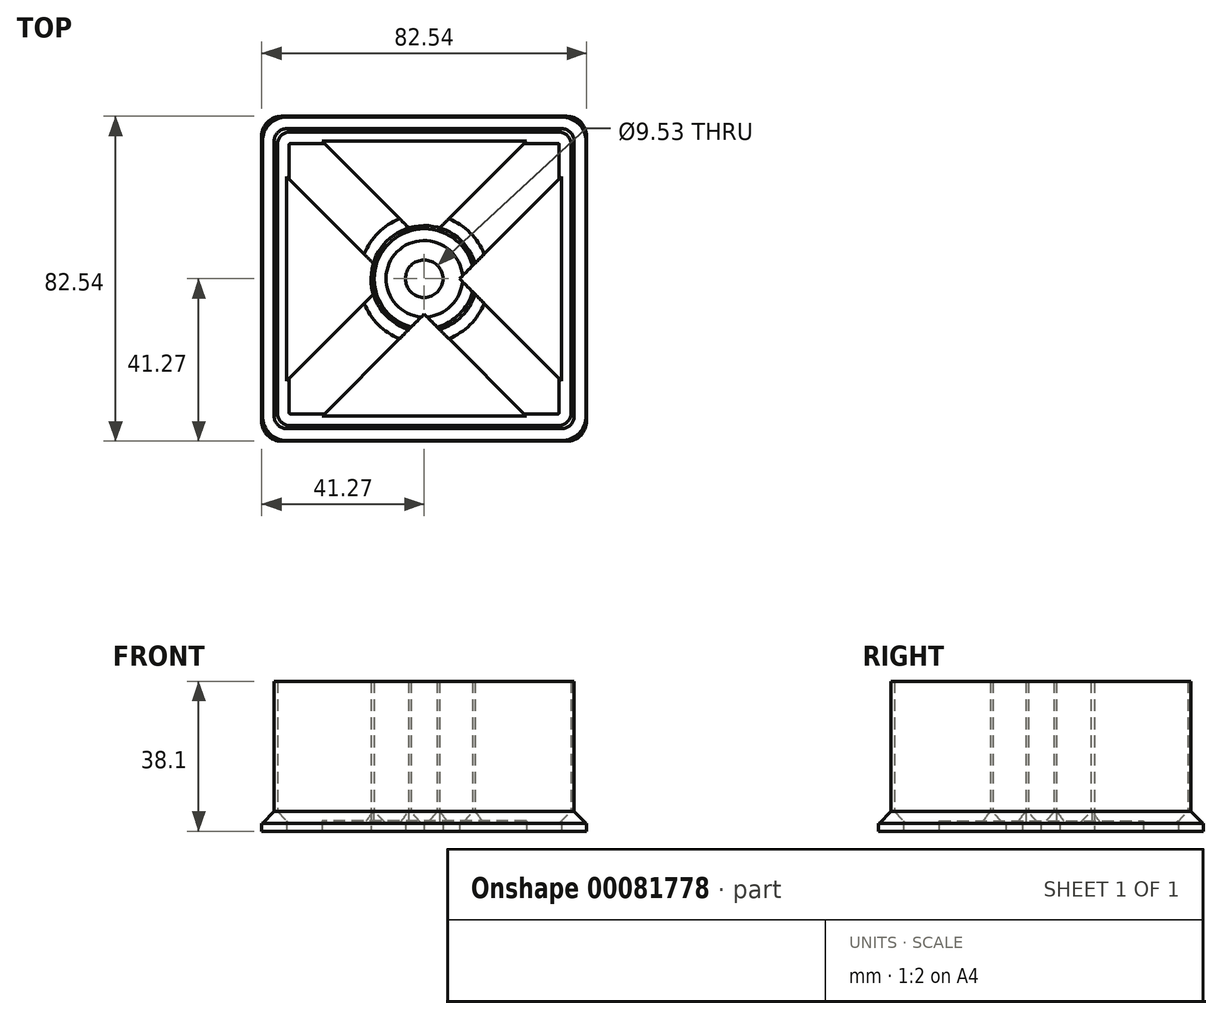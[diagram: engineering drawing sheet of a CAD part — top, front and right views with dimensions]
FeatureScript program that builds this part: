
annotation { "Feature Type Name" : "Feature", "Feature Type Description" : "" }
export const myFeature = defineFeature(function(context is Context, id is Id, definition is map)
    precondition{}
    {
        {
            var Q0;
            Q0=qCreatedBy(makeId("Top.planeOp"),FACE);
            var sketch = newSketch(context, id + "F0", { "sketchPlane" : qUnion([Q0])});
            skLineSegment(sketch, "E0.bottom", {"start": v(-34.92, 38.1) * mm, "end": v(34.93, 38.1) * mm});
            skLineSegment(sketch, "E0.top", {"start": v(-34.93, -38.1) * mm, "end": v(34.92, -38.1) * mm});
            skLineSegment(sketch, "E0.left", {"start": v(-38.1, 34.93) * mm, "end": v(-38.1, -34.93) * mm});
            skLineSegment(sketch, "E0.right", {"start": v(38.1, 34.93) * mm, "end": v(38.1, -34.93) * mm});
            skPoint(sketch, "E0.middle", {"position": v(0, 0) * mm});
            skCircle(sketch, "E1", {"center": v(0, 0) * mm, "radius": 12.7 * mm});
            skLineSegment(sketch, "E2.0", {"start": v(-37.3, 34.13) * mm, "end": v(-37.3, -34.13) * mm});
            skLineSegment(sketch, "E2.1", {"start": v(-34.13, 37.3) * mm, "end": v(34.13, 37.3) * mm});
            skLineSegment(sketch, "E2.2", {"start": v(37.3, 34.13) * mm, "end": v(37.3, -34.13) * mm});
            skLineSegment(sketch, "E2.3", {"start": v(-34.13, -37.3) * mm, "end": v(34.13, -37.3) * mm});
            skCircle(sketch, "E3.0", {"center": v(0, 0) * mm, "radius": 13.5 * mm});
            skLineSegment(sketch, "E4.0", {"start": v(-41.27, 41.27) * mm, "end": v(-41.28, -41.27) * mm});
            skLineSegment(sketch, "E4.1", {"start": v(-41.27, 41.27) * mm, "end": v(41.28, 41.27) * mm});
            skLineSegment(sketch, "E4.2", {"start": v(41.28, 41.27) * mm, "end": v(41.27, -41.27) * mm});
            skLineSegment(sketch, "E4.3", {"start": v(-41.28, -41.27) * mm, "end": v(41.27, -41.27) * mm});
            skLineSegment(sketch, "E5.0", {"start": v(-34.92, 34.92) * mm, "end": v(-34.93, -34.92) * mm});
            skLineSegment(sketch, "E5.1", {"start": v(-34.92, 34.92) * mm, "end": v(34.93, 34.92) * mm});
            skLineSegment(sketch, "E5.2", {"start": v(34.93, 34.92) * mm, "end": v(34.92, -34.92) * mm});
            skLineSegment(sketch, "E5.3", {"start": v(-34.93, -34.92) * mm, "end": v(34.92, -34.92) * mm});
            skLineSegment(sketch, "E6", {"start": v(-34.92, 34.92) * mm, "end": v(34.92, -34.92) * mm, "construction": true});
            skLineSegment(sketch, "E7.trimOffspring", {"start": v(-34.92, 25.94) * mm, "end": v(25.94, -34.92) * mm});
            skLineSegment(sketch, "E8.trimOffspring", {"start": v(-25.94, 34.92) * mm, "end": v(34.92, -25.94) * mm});
            skLineSegment(sketch, "E9", {"start": v(-34.92, -34.92) * mm, "end": v(34.92, 34.92) * mm, "construction": true});
            skLineSegment(sketch, "E10.0", {"start": v(-25.94, -34.93) * mm, "end": v(34.93, 25.94) * mm});
            skLineSegment(sketch, "E11.0", {"start": v(-34.93, -25.94) * mm, "end": v(25.94, 34.93) * mm});
            skCircle(sketch, "E12", {"center": v(0, 0) * mm, "radius": 4.76 * mm});
            skPoint(sketch, "E13.visualSharp", {"position": v(-38.1, -38.1) * mm});
            skArc(sketch, "E13.filletArc", {"start": v(-38.1, -34.93) * mm, "mid": v(-37.17, -37.17) * mm, "end": v(-34.93, -38.1) * mm});
            skPoint(sketch, "E14.visualSharp", {"position": v(-37.3, -37.3) * mm});
            skArc(sketch, "E14.filletArc", {"start": v(-37.3, -34.13) * mm, "mid": v(-36.38, -36.38) * mm, "end": v(-34.13, -37.3) * mm});
            skPoint(sketch, "E15.visualSharp", {"position": v(37.3, -37.3) * mm});
            skArc(sketch, "E15.filletArc", {"start": v(34.13, -37.3) * mm, "mid": v(36.38, -36.38) * mm, "end": v(37.3, -34.13) * mm});
            skPoint(sketch, "E16.visualSharp", {"position": v(38.1, -38.1) * mm});
            skArc(sketch, "E16.filletArc", {"start": v(34.92, -38.1) * mm, "mid": v(37.17, -37.17) * mm, "end": v(38.1, -34.93) * mm});
            skPoint(sketch, "E17.visualSharp", {"position": v(-37.3, 37.3) * mm});
            skArc(sketch, "E17.filletArc", {"start": v(-34.13, 37.3) * mm, "mid": v(-36.38, 36.38) * mm, "end": v(-37.3, 34.13) * mm});
            skPoint(sketch, "E18.visualSharp", {"position": v(-38.1, 38.1) * mm});
            skArc(sketch, "E18.filletArc", {"start": v(-34.92, 38.1) * mm, "mid": v(-37.17, 37.17) * mm, "end": v(-38.1, 34.93) * mm});
            skPoint(sketch, "E19.visualSharp", {"position": v(37.3, 37.3) * mm});
            skArc(sketch, "E19.filletArc", {"start": v(37.3, 34.13) * mm, "mid": v(36.38, 36.38) * mm, "end": v(34.13, 37.3) * mm});
            skPoint(sketch, "E20.visualSharp", {"position": v(38.1, 38.1) * mm});
            skArc(sketch, "E20.filletArc", {"start": v(38.1, 34.93) * mm, "mid": v(37.17, 37.17) * mm, "end": v(34.93, 38.1) * mm});
            skSolve(sketch);
        }
        {
            var Q0;
            Q0 = qSketchRegion(id + "F0", true);
            var Q1;
            {var subQ0=sQuery(id+"F0.wireOp",EDGE,"E7.trimOffspring");var subQ3=sQuery(id+"F0.wireOp",EDGE,"E3.0");var subQ4=makeQuery(id+"F0.imprint","INTERSECT",VERTEX,{"disambiguationData":[OD(1.0)],"derivedFrom":[subQ3,subQ0]});Q1=makeQuery(id+"F0.imprint","IMPRINT",FACE,{"disambiguationData":[TD([[makeQuery(id+"F0.imprint","IMPRINT",EDGE,{"disambiguationData":[TD([[subQ4,-1.0]])],"derivedFrom":subQ3}),-1.0]])]});}
            var Q2;
            {var subQ5=sQuery(id+"F0.wireOp",EDGE,"E3.0");var subQ7=sQuery(id+"F0.wireOp",EDGE,"E7.trimOffspring");var subQ9=makeQuery(id+"F0.imprint","INTERSECT",VERTEX,{"disambiguationData":[OD(0.0)],"derivedFrom":[subQ5,subQ7]});Q2=makeQuery(id+"F0.imprint","IMPRINT",FACE,{"disambiguationData":[TD([[makeQuery(id+"F0.imprint","IMPRINT",EDGE,{"disambiguationData":[TD([[subQ9,1.0]])],"derivedFrom":subQ5}),-1.0]])]});}
            var Q3;
            Q3=makeQuery(id+"F0.imprint","IMPRINT",FACE,{"disambiguationData":[TD([[makeQuery(id+"F0.imprint","IMPRINT",EDGE,{"derivedFrom":sQuery(id+"F0.wireOp",EDGE,"E2.0")}),1.0]])]});
            var Q4;
            Q4=makeQuery(id+"F0.imprint","IMPRINT",FACE,{"disambiguationData":[TD([[makeQuery(id+"F0.imprint","IMPRINT",EDGE,{"derivedFrom":sQuery(id+"F0.wireOp",EDGE,"E0.bottom")}),-1.0]])]});
            var Q5;
            {var subQ0=sQuery(id+"F0.wireOp",EDGE,"E8.trimOffspring");var subQ1=sQuery(id+"F0.wireOp",EDGE,"E1");var subQ2=makeQuery(id+"F0.imprint","INTERSECT",VERTEX,{"disambiguationData":[OD(0.0)],"derivedFrom":[subQ1,subQ0]});Q5=makeQuery(id+"F0.imprint","IMPRINT",FACE,{"disambiguationData":[TD([[makeQuery(id+"F0.imprint","IMPRINT",EDGE,{"disambiguationData":[TD([[subQ2,1.0]])],"derivedFrom":subQ1}),-1.0]])]});}
            var Q6;
            {var subQ0=sQuery(id+"F0.wireOp",EDGE,"E7.trimOffspring");var subQ1=sQuery(id+"F0.wireOp",EDGE,"E1");var subQ2=makeQuery(id+"F0.imprint","INTERSECT",VERTEX,{"disambiguationData":[OD(0.0)],"derivedFrom":[subQ1,subQ0]});Q6=makeQuery(id+"F0.imprint","IMPRINT",FACE,{"disambiguationData":[TD([[makeQuery(id+"F0.imprint","IMPRINT",EDGE,{"disambiguationData":[TD([[subQ2,-1.0]])],"derivedFrom":subQ1}),-1.0]])]});}
            var Q7;
            {var subQ0=sQuery(id+"F0.wireOp",EDGE,"E7.trimOffspring");var subQ1=sQuery(id+"F0.wireOp",EDGE,"E1");var subQ2=makeQuery(id+"F0.imprint","INTERSECT",VERTEX,{"disambiguationData":[OD(0.0)],"derivedFrom":[subQ1,subQ0]});Q7=makeQuery(id+"F0.imprint","IMPRINT",FACE,{"disambiguationData":[TD([[makeQuery(id+"F0.imprint","IMPRINT",EDGE,{"disambiguationData":[TD([[subQ2,1.0]])],"derivedFrom":subQ1}),1.0]])]});}
            var Q8;
            {var subQ0=sQuery(id+"F0.wireOp",EDGE,"E7.trimOffspring");var subQ1=sQuery(id+"F0.wireOp",EDGE,"E1");var subQ2=makeQuery(id+"F0.imprint","INTERSECT",VERTEX,{"disambiguationData":[OD(1.0)],"derivedFrom":[subQ1,subQ0]});Q8=makeQuery(id+"F0.imprint","IMPRINT",FACE,{"disambiguationData":[TD([[makeQuery(id+"F0.imprint","IMPRINT",EDGE,{"disambiguationData":[TD([[subQ2,-1.0]])],"derivedFrom":subQ1}),-1.0]])]});}
            var Q9;
            {var subQ0=sQuery(id+"F0.wireOp",EDGE,"E7.trimOffspring");var subQ1=sQuery(id+"F0.wireOp",EDGE,"E1");var subQ2=makeQuery(id+"F0.imprint","INTERSECT",VERTEX,{"disambiguationData":[OD(0.0)],"derivedFrom":[subQ1,subQ0]});Q9=makeQuery(id+"F0.imprint","IMPRINT",FACE,{"disambiguationData":[TD([[makeQuery(id+"F0.imprint","IMPRINT",EDGE,{"disambiguationData":[TD([[subQ2,1.0]])],"derivedFrom":subQ1}),-1.0]])]});}
            var Q10;
            {var subQ3=sQuery(id+"F0.wireOp",EDGE,"E3.0");var subQ7=sQuery(id+"F0.wireOp",EDGE,"E11.0");var subQ9=makeQuery(id+"F0.imprint","INTERSECT",VERTEX,{"disambiguationData":[OD(1.0)],"derivedFrom":[subQ3,subQ7]});Q10=makeQuery(id+"F0.imprint","IMPRINT",FACE,{"disambiguationData":[TD([[makeQuery(id+"F0.imprint","IMPRINT",EDGE,{"disambiguationData":[TD([[subQ9,-1.0]])],"derivedFrom":subQ3}),-1.0]])]});}
            var Q11;
            {var subQ3=sQuery(id+"F0.wireOp",EDGE,"E3.0");var subQ7=sQuery(id+"F0.wireOp",EDGE,"E11.0");var subQ9=makeQuery(id+"F0.imprint","INTERSECT",VERTEX,{"disambiguationData":[OD(0.0)],"derivedFrom":[subQ3,subQ7]});Q11=makeQuery(id+"F0.imprint","IMPRINT",FACE,{"disambiguationData":[TD([[makeQuery(id+"F0.imprint","IMPRINT",EDGE,{"disambiguationData":[TD([[subQ9,1.0]])],"derivedFrom":subQ3}),-1.0]])]});}
            var Q12;
            {var subQ0=sQuery(id+"F0.wireOp",EDGE,"E10.0");var subQ1=sQuery(id+"F0.wireOp",EDGE,"E1");var subQ2=makeQuery(id+"F0.imprint","INTERSECT",VERTEX,{"disambiguationData":[OD(1.0)],"derivedFrom":[subQ1,subQ0]});Q12=makeQuery(id+"F0.imprint","IMPRINT",FACE,{"disambiguationData":[TD([[makeQuery(id+"F0.imprint","IMPRINT",EDGE,{"disambiguationData":[TD([[subQ2,-1.0]])],"derivedFrom":subQ1}),-1.0]])]});}
            var Q13;
            {var subQ0=sQuery(id+"F0.wireOp",EDGE,"E10.0");var subQ1=sQuery(id+"F0.wireOp",EDGE,"E1");var subQ2=makeQuery(id+"F0.imprint","INTERSECT",VERTEX,{"disambiguationData":[OD(0.0)],"derivedFrom":[subQ1,subQ0]});Q13=makeQuery(id+"F0.imprint","IMPRINT",FACE,{"disambiguationData":[TD([[makeQuery(id+"F0.imprint","IMPRINT",EDGE,{"disambiguationData":[TD([[subQ2,1.0]])],"derivedFrom":subQ1}),-1.0]])]});}
            var Q14;
            {var subQ0=sQuery(id+"F0.wireOp",EDGE,"E11.0");var subQ1=sQuery(id+"F0.wireOp",EDGE,"E1");var subQ2=makeQuery(id+"F0.imprint","INTERSECT",VERTEX,{"disambiguationData":[OD(0.0)],"derivedFrom":[subQ1,subQ0]});Q14=makeQuery(id+"F0.imprint","IMPRINT",FACE,{"disambiguationData":[TD([[makeQuery(id+"F0.imprint","IMPRINT",EDGE,{"disambiguationData":[TD([[subQ2,1.0]])],"derivedFrom":subQ1}),-1.0]])]});}
            var Q15;
            {var subQ0=sQuery(id+"F0.wireOp",EDGE,"E11.0");var subQ1=sQuery(id+"F0.wireOp",EDGE,"E1");var subQ2=makeQuery(id+"F0.imprint","INTERSECT",VERTEX,{"disambiguationData":[OD(1.0)],"derivedFrom":[subQ1,subQ0]});Q15=makeQuery(id+"F0.imprint","IMPRINT",FACE,{"disambiguationData":[TD([[makeQuery(id+"F0.imprint","IMPRINT",EDGE,{"disambiguationData":[TD([[subQ2,-1.0]])],"derivedFrom":subQ1}),-1.0]])]});}
            var Q16;
            {var subQ0=sQuery(id+"F0.wireOp",EDGE,"E11.0");var subQ1=sQuery(id+"F0.wireOp",EDGE,"E1");var subQ2=makeQuery(id+"F0.imprint","INTERSECT",VERTEX,{"disambiguationData":[OD(1.0)],"derivedFrom":[subQ1,subQ0]});Q16=makeQuery(id+"F0.imprint","IMPRINT",FACE,{"disambiguationData":[TD([[makeQuery(id+"F0.imprint","IMPRINT",EDGE,{"disambiguationData":[TD([[subQ2,-1.0]])],"derivedFrom":subQ1}),1.0]])]});}
            var Q17;
            {var subQ0=sQuery(id+"F0.wireOp",EDGE,"E11.0");var subQ1=sQuery(id+"F0.wireOp",EDGE,"E7.trimOffspring");var subQ2=makeQuery(id+"F0.imprint","INTERSECT",VERTEX,{"derivedFrom":[subQ1,subQ0]});Q17=makeQuery(id+"F0.imprint","IMPRINT",FACE,{"disambiguationData":[TD([[makeQuery(id+"F0.imprint","IMPRINT",EDGE,{"disambiguationData":[TD([[subQ2,-1.0]])],"derivedFrom":subQ1}),1.0]])]});}
            var Q18;
            {var subQ0=sQuery(id+"F0.wireOp",EDGE,"E11.0");var subQ1=sQuery(id+"F0.wireOp",EDGE,"E1");var subQ2=makeQuery(id+"F0.imprint","INTERSECT",VERTEX,{"disambiguationData":[OD(0.0)],"derivedFrom":[subQ1,subQ0]});Q18=makeQuery(id+"F0.imprint","IMPRINT",FACE,{"disambiguationData":[TD([[makeQuery(id+"F0.imprint","IMPRINT",EDGE,{"disambiguationData":[TD([[subQ2,1.0]])],"derivedFrom":subQ1}),1.0]])]});}
            var Q19;
            {var subQ0=sQuery(id+"F0.wireOp",EDGE,"E7.trimOffspring");var subQ1=sQuery(id+"F0.wireOp",EDGE,"E1");var subQ2=makeQuery(id+"F0.imprint","INTERSECT",VERTEX,{"disambiguationData":[OD(1.0)],"derivedFrom":[subQ1,subQ0]});Q19=makeQuery(id+"F0.imprint","IMPRINT",FACE,{"disambiguationData":[TD([[makeQuery(id+"F0.imprint","IMPRINT",EDGE,{"disambiguationData":[TD([[subQ2,-1.0]])],"derivedFrom":subQ1}),1.0]])]});}
            var Q20;
            {var subQ0=sQuery(id+"F0.wireOp",EDGE,"E7.trimOffspring");var subQ1=sQuery(id+"F0.wireOp",EDGE,"E1");var subQ2=makeQuery(id+"F0.imprint","INTERSECT",VERTEX,{"disambiguationData":[OD(0.0)],"derivedFrom":[subQ1,subQ0]});Q20=makeQuery(id+"F0.imprint","IMPRINT",FACE,{"disambiguationData":[TD([[makeQuery(id+"F0.imprint","IMPRINT",EDGE,{"disambiguationData":[TD([[subQ2,-1.0]])],"derivedFrom":subQ1}),1.0]])]});}
            var Q21;
            {var subQ0=sQuery(id+"F0.wireOp",EDGE,"E11.0");var subQ1=sQuery(id+"F0.wireOp",EDGE,"E1");var subQ2=makeQuery(id+"F0.imprint","INTERSECT",VERTEX,{"disambiguationData":[OD(0.0)],"derivedFrom":[subQ1,subQ0]});Q21=makeQuery(id+"F0.imprint","IMPRINT",FACE,{"disambiguationData":[TD([[makeQuery(id+"F0.imprint","IMPRINT",EDGE,{"disambiguationData":[TD([[subQ2,-1.0]])],"derivedFrom":subQ1}),1.0]])]});}
            var Q22;
            {var subQ0=sQuery(id+"F0.wireOp",EDGE,"E10.0");var subQ1=sQuery(id+"F0.wireOp",EDGE,"E1");var subQ2=makeQuery(id+"F0.imprint","INTERSECT",VERTEX,{"disambiguationData":[OD(0.0)],"derivedFrom":[subQ1,subQ0]});Q22=makeQuery(id+"F0.imprint","IMPRINT",FACE,{"disambiguationData":[TD([[makeQuery(id+"F0.imprint","IMPRINT",EDGE,{"disambiguationData":[TD([[subQ2,1.0]])],"derivedFrom":subQ1}),1.0]])]});}
            var Q23;
            {var subQ0=sQuery(id+"F0.wireOp",EDGE,"E10.0");var subQ1=sQuery(id+"F0.wireOp",EDGE,"E1");var subQ2=makeQuery(id+"F0.imprint","INTERSECT",VERTEX,{"disambiguationData":[OD(1.0)],"derivedFrom":[subQ1,subQ0]});Q23=makeQuery(id+"F0.imprint","IMPRINT",FACE,{"disambiguationData":[TD([[makeQuery(id+"F0.imprint","IMPRINT",EDGE,{"disambiguationData":[TD([[subQ2,-1.0]])],"derivedFrom":subQ1}),1.0]])]});}
            extrude(context, id + "F1", {"entities" : qUnion([Q0, Q1, Q2, Q3, Q4, Q5, Q6, Q7, Q8, Q9, Q10, Q11, Q12, Q13, Q14, Q15, Q16, Q17, Q18, Q19, Q20, Q21, Q22, Q23]), "depth" : 2 * mm});
        }
        {
            var Q0;
            Q0=makeQuery(id+"F0.imprint","IMPRINT",FACE,{"disambiguationData":[TD([[makeQuery(id+"F0.imprint","IMPRINT",EDGE,{"derivedFrom":sQuery(id+"F0.wireOp",EDGE,"E0.bottom")}),-1.0]])]});
            var Q1;
            {var subQ0=sQuery(id+"F0.wireOp",EDGE,"E7.trimOffspring");var subQ1=sQuery(id+"F0.wireOp",EDGE,"E1");var subQ2=makeQuery(id+"F0.imprint","INTERSECT",VERTEX,{"disambiguationData":[OD(0.0)],"derivedFrom":[subQ1,subQ0]});Q1=makeQuery(id+"F0.imprint","IMPRINT",FACE,{"disambiguationData":[TD([[makeQuery(id+"F0.imprint","IMPRINT",EDGE,{"disambiguationData":[TD([[subQ2,-1.0]])],"derivedFrom":subQ1}),-1.0]])]});}
            var Q2;
            {var subQ0=sQuery(id+"F0.wireOp",EDGE,"E7.trimOffspring");var subQ1=sQuery(id+"F0.wireOp",EDGE,"E1");var subQ2=makeQuery(id+"F0.imprint","INTERSECT",VERTEX,{"disambiguationData":[OD(1.0)],"derivedFrom":[subQ1,subQ0]});Q2=makeQuery(id+"F0.imprint","IMPRINT",FACE,{"disambiguationData":[TD([[makeQuery(id+"F0.imprint","IMPRINT",EDGE,{"disambiguationData":[TD([[subQ2,-1.0]])],"derivedFrom":subQ1}),-1.0]])]});}
            var Q3;
            {var subQ0=sQuery(id+"F0.wireOp",EDGE,"E8.trimOffspring");var subQ1=sQuery(id+"F0.wireOp",EDGE,"E1");var subQ2=makeQuery(id+"F0.imprint","INTERSECT",VERTEX,{"disambiguationData":[OD(0.0)],"derivedFrom":[subQ1,subQ0]});Q3=makeQuery(id+"F0.imprint","IMPRINT",FACE,{"disambiguationData":[TD([[makeQuery(id+"F0.imprint","IMPRINT",EDGE,{"disambiguationData":[TD([[subQ2,1.0]])],"derivedFrom":subQ1}),-1.0]])]});}
            var Q4;
            {var subQ0=sQuery(id+"F0.wireOp",EDGE,"E7.trimOffspring");var subQ1=sQuery(id+"F0.wireOp",EDGE,"E1");var subQ2=makeQuery(id+"F0.imprint","INTERSECT",VERTEX,{"disambiguationData":[OD(0.0)],"derivedFrom":[subQ1,subQ0]});Q4=makeQuery(id+"F0.imprint","IMPRINT",FACE,{"disambiguationData":[TD([[makeQuery(id+"F0.imprint","IMPRINT",EDGE,{"disambiguationData":[TD([[subQ2,1.0]])],"derivedFrom":subQ1}),-1.0]])]});}
            var Q5;
            {var subQ0=sQuery(id+"F0.wireOp",EDGE,"E11.0");var subQ1=sQuery(id+"F0.wireOp",EDGE,"E1");var subQ2=makeQuery(id+"F0.imprint","INTERSECT",VERTEX,{"disambiguationData":[OD(1.0)],"derivedFrom":[subQ1,subQ0]});Q5=makeQuery(id+"F0.imprint","IMPRINT",FACE,{"disambiguationData":[TD([[makeQuery(id+"F0.imprint","IMPRINT",EDGE,{"disambiguationData":[TD([[subQ2,-1.0]])],"derivedFrom":subQ1}),-1.0]])]});}
            var Q6;
            {var subQ0=sQuery(id+"F0.wireOp",EDGE,"E10.0");var subQ1=sQuery(id+"F0.wireOp",EDGE,"E1");var subQ2=makeQuery(id+"F0.imprint","INTERSECT",VERTEX,{"disambiguationData":[OD(1.0)],"derivedFrom":[subQ1,subQ0]});Q6=makeQuery(id+"F0.imprint","IMPRINT",FACE,{"disambiguationData":[TD([[makeQuery(id+"F0.imprint","IMPRINT",EDGE,{"disambiguationData":[TD([[subQ2,-1.0]])],"derivedFrom":subQ1}),-1.0]])]});}
            var Q7;
            {var subQ0=sQuery(id+"F0.wireOp",EDGE,"E10.0");var subQ1=sQuery(id+"F0.wireOp",EDGE,"E1");var subQ2=makeQuery(id+"F0.imprint","INTERSECT",VERTEX,{"disambiguationData":[OD(0.0)],"derivedFrom":[subQ1,subQ0]});Q7=makeQuery(id+"F0.imprint","IMPRINT",FACE,{"disambiguationData":[TD([[makeQuery(id+"F0.imprint","IMPRINT",EDGE,{"disambiguationData":[TD([[subQ2,1.0]])],"derivedFrom":subQ1}),-1.0]])]});}
            var Q8;
            {var subQ0=sQuery(id+"F0.wireOp",EDGE,"E11.0");var subQ1=sQuery(id+"F0.wireOp",EDGE,"E1");var subQ2=makeQuery(id+"F0.imprint","INTERSECT",VERTEX,{"disambiguationData":[OD(0.0)],"derivedFrom":[subQ1,subQ0]});Q8=makeQuery(id+"F0.imprint","IMPRINT",FACE,{"disambiguationData":[TD([[makeQuery(id+"F0.imprint","IMPRINT",EDGE,{"disambiguationData":[TD([[subQ2,1.0]])],"derivedFrom":subQ1}),-1.0]])]});}
            extrude(context, id + "F2", {"entities" : qUnion([Q0, Q1, Q2, Q3, Q4, Q5, Q6, Q7, Q8]), "operationType" : NewBodyOperationType.ADD, "depth" : 38.1 * mm});
        }
        {
            var Q0;
            Q0=makeQuery(id+"F1.opExtrude","SWEPT_EDGE",EDGE,{"disambiguationData":[OSD([sQuery(id+"F0.wireOp",EDGE,"E4.1"),sQuery(id+"F0.wireOp",EDGE,"E4.2")])]});
            var Q1;
            Q1=makeQuery(id+"F1.opExtrude","SWEPT_EDGE",EDGE,{"disambiguationData":[OSD([sQuery(id+"F0.wireOp",EDGE,"E4.2"),sQuery(id+"F0.wireOp",EDGE,"E4.3")])]});
            var Q2;
            Q2=makeQuery(id+"F1.opExtrude","SWEPT_EDGE",EDGE,{"disambiguationData":[OSD([sQuery(id+"F0.wireOp",EDGE,"E4.0"),sQuery(id+"F0.wireOp",EDGE,"E4.3")])]});
            var Q3;
            Q3=makeQuery(id+"F1.opExtrude","SWEPT_EDGE",EDGE,{"disambiguationData":[OSD([sQuery(id+"F0.wireOp",EDGE,"E4.0"),sQuery(id+"F0.wireOp",EDGE,"E4.1")])]});
            fillet(context, id + "F3", {"entities" : qUnion([Q0, Q1, Q2, Q3]), "radius" : 5.08 * mm, "tangentPropagation" : true, "allowEdgeOverflow" : false});
        }
        {
            var Q0;
            Q0=makeQuery(id+"F2.boolean.opBoolean","INTERSECT",EDGE,{"derivedFrom":[makeQuery(id+"F1.opExtrude","CAP_FACE",FACE,{"disambiguationData":[OSD([sQuery(id+"F0.wireOp",EDGE,"E1"),sQuery(id+"F0.wireOp",EDGE,"E3.0"),sQuery(id+"F0.wireOp",EDGE,"E4.0"),sQuery(id+"F0.wireOp",EDGE,"E4.1"),sQuery(id+"F0.wireOp",EDGE,"E4.2"),sQuery(id+"F0.wireOp",EDGE,"E4.3"),sQuery(id+"F0.wireOp",EDGE,"E5.0"),sQuery(id+"F0.wireOp",EDGE,"E5.1"),sQuery(id+"F0.wireOp",EDGE,"E5.2"),sQuery(id+"F0.wireOp",EDGE,"E5.3"),sQuery(id+"F0.wireOp",EDGE,"E7.trimOffspring"),sQuery(id+"F0.wireOp",EDGE,"E8.trimOffspring"),sQuery(id+"F0.wireOp",EDGE,"E10.0"),sQuery(id+"F0.wireOp",EDGE,"E11.0")])],"isStart":false}),makeQuery(id+"F2.opExtrude","SWEPT_FACE",FACE,{"disambiguationData":[OSD([sQuery(id+"F0.wireOp",EDGE,"E2.0")])]})]});
            var Q1;
            Q1=makeQuery(id+"F2.boolean.opBoolean","INTERSECT",EDGE,{"derivedFrom":[makeQuery(id+"F1.opExtrude","CAP_FACE",FACE,{"disambiguationData":[OSD([sQuery(id+"F0.wireOp",EDGE,"E1"),sQuery(id+"F0.wireOp",EDGE,"E3.0"),sQuery(id+"F0.wireOp",EDGE,"E4.0"),sQuery(id+"F0.wireOp",EDGE,"E4.1"),sQuery(id+"F0.wireOp",EDGE,"E4.2"),sQuery(id+"F0.wireOp",EDGE,"E4.3"),sQuery(id+"F0.wireOp",EDGE,"E5.0"),sQuery(id+"F0.wireOp",EDGE,"E5.1"),sQuery(id+"F0.wireOp",EDGE,"E5.2"),sQuery(id+"F0.wireOp",EDGE,"E5.3"),sQuery(id+"F0.wireOp",EDGE,"E7.trimOffspring"),sQuery(id+"F0.wireOp",EDGE,"E8.trimOffspring"),sQuery(id+"F0.wireOp",EDGE,"E10.0"),sQuery(id+"F0.wireOp",EDGE,"E11.0")])],"isStart":false}),makeQuery(id+"F2.opExtrude","SWEPT_FACE",FACE,{"disambiguationData":[OSD([sQuery(id+"F0.wireOp",EDGE,"E2.1")])]})]});
            var Q2;
            Q2=makeQuery(id+"F2.boolean.opBoolean","INTERSECT",EDGE,{"derivedFrom":[makeQuery(id+"F1.opExtrude","CAP_FACE",FACE,{"disambiguationData":[OSD([sQuery(id+"F0.wireOp",EDGE,"E1"),sQuery(id+"F0.wireOp",EDGE,"E3.0"),sQuery(id+"F0.wireOp",EDGE,"E4.0"),sQuery(id+"F0.wireOp",EDGE,"E4.1"),sQuery(id+"F0.wireOp",EDGE,"E4.2"),sQuery(id+"F0.wireOp",EDGE,"E4.3"),sQuery(id+"F0.wireOp",EDGE,"E5.0"),sQuery(id+"F0.wireOp",EDGE,"E5.1"),sQuery(id+"F0.wireOp",EDGE,"E5.2"),sQuery(id+"F0.wireOp",EDGE,"E5.3"),sQuery(id+"F0.wireOp",EDGE,"E7.trimOffspring"),sQuery(id+"F0.wireOp",EDGE,"E8.trimOffspring"),sQuery(id+"F0.wireOp",EDGE,"E10.0"),sQuery(id+"F0.wireOp",EDGE,"E11.0")])],"isStart":false}),makeQuery(id+"F2.opExtrude","SWEPT_FACE",FACE,{"disambiguationData":[OSD([sQuery(id+"F0.wireOp",EDGE,"E2.2")])]})]});
            var Q3;
            Q3=makeQuery(id+"F2.boolean.opBoolean","INTERSECT",EDGE,{"derivedFrom":[makeQuery(id+"F1.opExtrude","CAP_FACE",FACE,{"disambiguationData":[OSD([sQuery(id+"F0.wireOp",EDGE,"E1"),sQuery(id+"F0.wireOp",EDGE,"E3.0"),sQuery(id+"F0.wireOp",EDGE,"E4.0"),sQuery(id+"F0.wireOp",EDGE,"E4.1"),sQuery(id+"F0.wireOp",EDGE,"E4.2"),sQuery(id+"F0.wireOp",EDGE,"E4.3"),sQuery(id+"F0.wireOp",EDGE,"E5.0"),sQuery(id+"F0.wireOp",EDGE,"E5.1"),sQuery(id+"F0.wireOp",EDGE,"E5.2"),sQuery(id+"F0.wireOp",EDGE,"E5.3"),sQuery(id+"F0.wireOp",EDGE,"E7.trimOffspring"),sQuery(id+"F0.wireOp",EDGE,"E8.trimOffspring"),sQuery(id+"F0.wireOp",EDGE,"E10.0"),sQuery(id+"F0.wireOp",EDGE,"E11.0")])],"isStart":false}),makeQuery(id+"F2.opExtrude","SWEPT_FACE",FACE,{"disambiguationData":[OSD([sQuery(id+"F0.wireOp",EDGE,"E2.3")])]})]});
            var Q4;
            {var subQ0=sQuery(id+"F0.wireOp",EDGE,"E3.0");Q4=makeQuery(id+"F2.boolean.opBoolean","INTERSECT",EDGE,{"disambiguationData":[OD(2.0)],"derivedFrom":[makeQuery(id+"F1.opExtrude","CAP_FACE",FACE,{"disambiguationData":[OSD([sQuery(id+"F0.wireOp",EDGE,"E1"),subQ0,sQuery(id+"F0.wireOp",EDGE,"E4.0"),sQuery(id+"F0.wireOp",EDGE,"E4.1"),sQuery(id+"F0.wireOp",EDGE,"E4.2"),sQuery(id+"F0.wireOp",EDGE,"E4.3"),sQuery(id+"F0.wireOp",EDGE,"E5.0"),sQuery(id+"F0.wireOp",EDGE,"E5.1"),sQuery(id+"F0.wireOp",EDGE,"E5.2"),sQuery(id+"F0.wireOp",EDGE,"E5.3"),sQuery(id+"F0.wireOp",EDGE,"E7.trimOffspring"),sQuery(id+"F0.wireOp",EDGE,"E8.trimOffspring"),sQuery(id+"F0.wireOp",EDGE,"E10.0"),sQuery(id+"F0.wireOp",EDGE,"E11.0")])],"isStart":false}),makeQuery(id+"F2.opExtrude","SWEPT_FACE",FACE,{"disambiguationData":[OSD([subQ0])]})]});}
            var Q5;
            {var subQ0=sQuery(id+"F0.wireOp",EDGE,"E3.0");Q5=makeQuery(id+"F2.boolean.opBoolean","INTERSECT",EDGE,{"disambiguationData":[OD(3.0)],"derivedFrom":[makeQuery(id+"F1.opExtrude","CAP_FACE",FACE,{"disambiguationData":[OSD([sQuery(id+"F0.wireOp",EDGE,"E1"),subQ0,sQuery(id+"F0.wireOp",EDGE,"E4.0"),sQuery(id+"F0.wireOp",EDGE,"E4.1"),sQuery(id+"F0.wireOp",EDGE,"E4.2"),sQuery(id+"F0.wireOp",EDGE,"E4.3"),sQuery(id+"F0.wireOp",EDGE,"E5.0"),sQuery(id+"F0.wireOp",EDGE,"E5.1"),sQuery(id+"F0.wireOp",EDGE,"E5.2"),sQuery(id+"F0.wireOp",EDGE,"E5.3"),sQuery(id+"F0.wireOp",EDGE,"E7.trimOffspring"),sQuery(id+"F0.wireOp",EDGE,"E8.trimOffspring"),sQuery(id+"F0.wireOp",EDGE,"E10.0"),sQuery(id+"F0.wireOp",EDGE,"E11.0")])],"isStart":false}),makeQuery(id+"F2.opExtrude","SWEPT_FACE",FACE,{"disambiguationData":[OSD([subQ0])]})]});}
            var Q6;
            {var subQ0=sQuery(id+"F0.wireOp",EDGE,"E3.0");Q6=makeQuery(id+"F2.boolean.opBoolean","INTERSECT",EDGE,{"disambiguationData":[OD(0.0)],"derivedFrom":[makeQuery(id+"F1.opExtrude","CAP_FACE",FACE,{"disambiguationData":[OSD([sQuery(id+"F0.wireOp",EDGE,"E1"),subQ0,sQuery(id+"F0.wireOp",EDGE,"E4.0"),sQuery(id+"F0.wireOp",EDGE,"E4.1"),sQuery(id+"F0.wireOp",EDGE,"E4.2"),sQuery(id+"F0.wireOp",EDGE,"E4.3"),sQuery(id+"F0.wireOp",EDGE,"E5.0"),sQuery(id+"F0.wireOp",EDGE,"E5.1"),sQuery(id+"F0.wireOp",EDGE,"E5.2"),sQuery(id+"F0.wireOp",EDGE,"E5.3"),sQuery(id+"F0.wireOp",EDGE,"E7.trimOffspring"),sQuery(id+"F0.wireOp",EDGE,"E8.trimOffspring"),sQuery(id+"F0.wireOp",EDGE,"E10.0"),sQuery(id+"F0.wireOp",EDGE,"E11.0")])],"isStart":false}),makeQuery(id+"F2.opExtrude","SWEPT_FACE",FACE,{"disambiguationData":[OSD([subQ0])]})]});}
            var Q7;
            {var subQ0=sQuery(id+"F0.wireOp",EDGE,"E3.0");Q7=makeQuery(id+"F2.boolean.opBoolean","INTERSECT",EDGE,{"disambiguationData":[OD(1.0)],"derivedFrom":[makeQuery(id+"F1.opExtrude","CAP_FACE",FACE,{"disambiguationData":[OSD([sQuery(id+"F0.wireOp",EDGE,"E1"),subQ0,sQuery(id+"F0.wireOp",EDGE,"E4.0"),sQuery(id+"F0.wireOp",EDGE,"E4.1"),sQuery(id+"F0.wireOp",EDGE,"E4.2"),sQuery(id+"F0.wireOp",EDGE,"E4.3"),sQuery(id+"F0.wireOp",EDGE,"E5.0"),sQuery(id+"F0.wireOp",EDGE,"E5.1"),sQuery(id+"F0.wireOp",EDGE,"E5.2"),sQuery(id+"F0.wireOp",EDGE,"E5.3"),sQuery(id+"F0.wireOp",EDGE,"E7.trimOffspring"),sQuery(id+"F0.wireOp",EDGE,"E8.trimOffspring"),sQuery(id+"F0.wireOp",EDGE,"E10.0"),sQuery(id+"F0.wireOp",EDGE,"E11.0")])],"isStart":false}),makeQuery(id+"F2.opExtrude","SWEPT_FACE",FACE,{"disambiguationData":[OSD([subQ0])]})]});}
            chamfer(context, id + "F4", {"entities" : qUnion([Q0, Q1, Q2, Q3, Q4, Q5, Q6, Q7]), "width" : 3 * mm, "tangentPropagation" : true});
        }
        {
            var Q0;
            Q0=makeQuery(id+"F2.boolean.opBoolean","INTERSECT",EDGE,{"derivedFrom":[makeQuery(id+"F1.opExtrude","CAP_FACE",FACE,{"disambiguationData":[OSD([sQuery(id+"F0.wireOp",EDGE,"E1"),sQuery(id+"F0.wireOp",EDGE,"E3.0"),sQuery(id+"F0.wireOp",EDGE,"E4.0"),sQuery(id+"F0.wireOp",EDGE,"E4.1"),sQuery(id+"F0.wireOp",EDGE,"E4.2"),sQuery(id+"F0.wireOp",EDGE,"E4.3"),sQuery(id+"F0.wireOp",EDGE,"E5.0"),sQuery(id+"F0.wireOp",EDGE,"E5.1"),sQuery(id+"F0.wireOp",EDGE,"E5.2"),sQuery(id+"F0.wireOp",EDGE,"E5.3"),sQuery(id+"F0.wireOp",EDGE,"E7.trimOffspring"),sQuery(id+"F0.wireOp",EDGE,"E8.trimOffspring"),sQuery(id+"F0.wireOp",EDGE,"E10.0"),sQuery(id+"F0.wireOp",EDGE,"E11.0")])],"isStart":false}),makeQuery(id+"F2.opExtrude","SWEPT_FACE",FACE,{"disambiguationData":[OSD([sQuery(id+"F0.wireOp",EDGE,"E0.left")])]})]});
            var Q1;
            Q1=makeQuery(id+"F2.boolean.opBoolean","INTERSECT",EDGE,{"derivedFrom":[makeQuery(id+"F1.opExtrude","CAP_FACE",FACE,{"disambiguationData":[OSD([sQuery(id+"F0.wireOp",EDGE,"E1"),sQuery(id+"F0.wireOp",EDGE,"E3.0"),sQuery(id+"F0.wireOp",EDGE,"E4.0"),sQuery(id+"F0.wireOp",EDGE,"E4.1"),sQuery(id+"F0.wireOp",EDGE,"E4.2"),sQuery(id+"F0.wireOp",EDGE,"E4.3"),sQuery(id+"F0.wireOp",EDGE,"E5.0"),sQuery(id+"F0.wireOp",EDGE,"E5.1"),sQuery(id+"F0.wireOp",EDGE,"E5.2"),sQuery(id+"F0.wireOp",EDGE,"E5.3"),sQuery(id+"F0.wireOp",EDGE,"E7.trimOffspring"),sQuery(id+"F0.wireOp",EDGE,"E8.trimOffspring"),sQuery(id+"F0.wireOp",EDGE,"E10.0"),sQuery(id+"F0.wireOp",EDGE,"E11.0")])],"isStart":false}),makeQuery(id+"F2.opExtrude","SWEPT_FACE",FACE,{"disambiguationData":[OSD([sQuery(id+"F0.wireOp",EDGE,"E0.top")])]})]});
            var Q2;
            Q2=makeQuery(id+"F2.boolean.opBoolean","INTERSECT",EDGE,{"derivedFrom":[makeQuery(id+"F1.opExtrude","CAP_FACE",FACE,{"disambiguationData":[OSD([sQuery(id+"F0.wireOp",EDGE,"E1"),sQuery(id+"F0.wireOp",EDGE,"E3.0"),sQuery(id+"F0.wireOp",EDGE,"E4.0"),sQuery(id+"F0.wireOp",EDGE,"E4.1"),sQuery(id+"F0.wireOp",EDGE,"E4.2"),sQuery(id+"F0.wireOp",EDGE,"E4.3"),sQuery(id+"F0.wireOp",EDGE,"E5.0"),sQuery(id+"F0.wireOp",EDGE,"E5.1"),sQuery(id+"F0.wireOp",EDGE,"E5.2"),sQuery(id+"F0.wireOp",EDGE,"E5.3"),sQuery(id+"F0.wireOp",EDGE,"E7.trimOffspring"),sQuery(id+"F0.wireOp",EDGE,"E8.trimOffspring"),sQuery(id+"F0.wireOp",EDGE,"E10.0"),sQuery(id+"F0.wireOp",EDGE,"E11.0")])],"isStart":false}),makeQuery(id+"F2.opExtrude","SWEPT_FACE",FACE,{"disambiguationData":[OSD([sQuery(id+"F0.wireOp",EDGE,"E0.right")])]})]});
            var Q3;
            Q3=makeQuery(id+"F2.boolean.opBoolean","INTERSECT",EDGE,{"derivedFrom":[makeQuery(id+"F1.opExtrude","CAP_FACE",FACE,{"disambiguationData":[OSD([sQuery(id+"F0.wireOp",EDGE,"E1"),sQuery(id+"F0.wireOp",EDGE,"E3.0"),sQuery(id+"F0.wireOp",EDGE,"E4.0"),sQuery(id+"F0.wireOp",EDGE,"E4.1"),sQuery(id+"F0.wireOp",EDGE,"E4.2"),sQuery(id+"F0.wireOp",EDGE,"E4.3"),sQuery(id+"F0.wireOp",EDGE,"E5.0"),sQuery(id+"F0.wireOp",EDGE,"E5.1"),sQuery(id+"F0.wireOp",EDGE,"E5.2"),sQuery(id+"F0.wireOp",EDGE,"E5.3"),sQuery(id+"F0.wireOp",EDGE,"E7.trimOffspring"),sQuery(id+"F0.wireOp",EDGE,"E8.trimOffspring"),sQuery(id+"F0.wireOp",EDGE,"E10.0"),sQuery(id+"F0.wireOp",EDGE,"E11.0")])],"isStart":false}),makeQuery(id+"F2.opExtrude","SWEPT_FACE",FACE,{"disambiguationData":[OSD([sQuery(id+"F0.wireOp",EDGE,"E0.bottom")])]})]});
            chamfer(context, id + "F5", {"entities" : qUnion([Q0, Q1, Q2, Q3]), "width" : 3 * mm, "tangentPropagation" : true});
        }
        {
            var Q0;
            Q0=makeQuery(id+"F2.boolean.opBoolean","INTERSECT",EDGE,{"derivedFrom":[makeQuery(id+"F1.opExtrude","CAP_FACE",FACE,{"disambiguationData":[OSD([sQuery(id+"F0.wireOp",EDGE,"E3.0"),sQuery(id+"F0.wireOp",EDGE,"E4.0"),sQuery(id+"F0.wireOp",EDGE,"E4.1"),sQuery(id+"F0.wireOp",EDGE,"E4.2"),sQuery(id+"F0.wireOp",EDGE,"E4.3"),sQuery(id+"F0.wireOp",EDGE,"E5.0"),sQuery(id+"F0.wireOp",EDGE,"E5.1"),sQuery(id+"F0.wireOp",EDGE,"E5.2"),sQuery(id+"F0.wireOp",EDGE,"E5.3"),sQuery(id+"F0.wireOp",EDGE,"E7.trimOffspring"),sQuery(id+"F0.wireOp",EDGE,"E8.trimOffspring"),sQuery(id+"F0.wireOp",EDGE,"E10.0"),sQuery(id+"F0.wireOp",EDGE,"E11.0"),sQuery(id+"F0.wireOp",EDGE,"E12")])],"isStart":false}),makeQuery(id+"F2.opExtrude","SWEPT_FACE",FACE,{"disambiguationData":[OSD([sQuery(id+"F0.wireOp",EDGE,"E1")])]})]});
            chamfer(context, id + "F6", {"entities" : qUnion([Q0]), "width" : 3 * mm, "tangentPropagation" : true});
        }
    });
